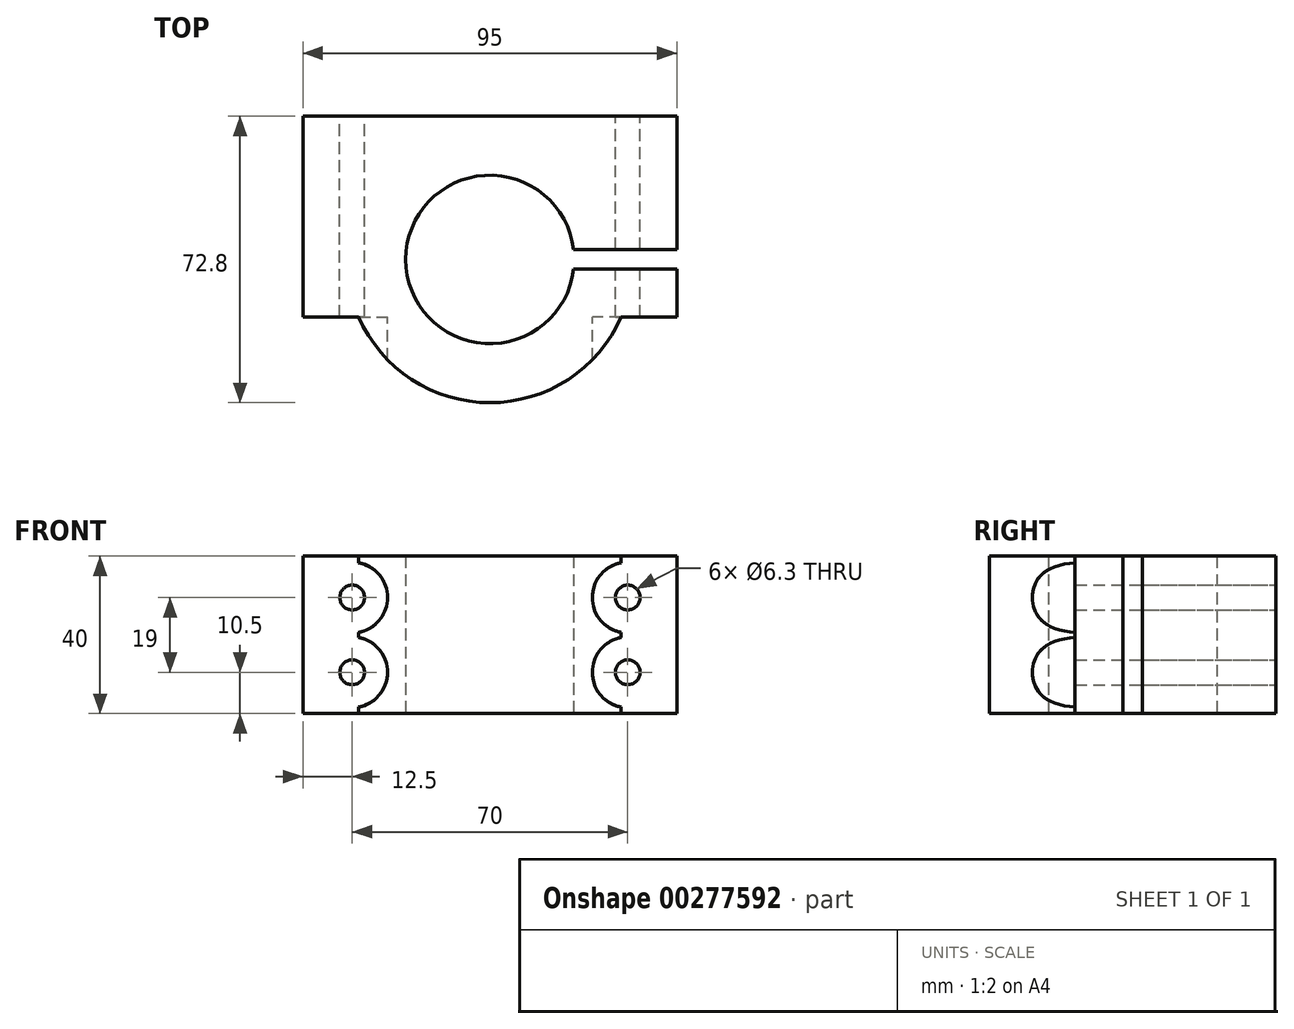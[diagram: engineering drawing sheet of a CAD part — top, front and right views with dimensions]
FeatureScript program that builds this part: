
annotation { "Feature Type Name" : "Feature", "Feature Type Description" : "" }
export const myFeature = defineFeature(function(context is Context, id is Id, definition is map)
    precondition{}
    {
        {
            var Q0;
            Q0=qCreatedBy(makeId("Top.planeOp"),FACE);
            var sketch = newSketch(context, id + "F0", { "sketchPlane" : qUnion([Q0])});
            skLineSegment(sketch, "E0.bottom", {"start": v(47.5, -25.5) * mm, "end": v(-47.5, -25.5) * mm});
            skLineSegment(sketch, "E0.top", {"start": v(47.5, 25.5) * mm, "end": v(-47.5, 25.5) * mm});
            skLineSegment(sketch, "E0.left", {"start": v(47.5, -25.5) * mm, "end": v(47.5, 25.5) * mm});
            skLineSegment(sketch, "E0.right", {"start": v(-47.5, -25.5) * mm, "end": v(-47.5, 25.5) * mm});
            skPoint(sketch, "E0.middle", {"position": v(0, 0) * mm});
            skCircle(sketch, "E1", {"center": v(0, -10.9) * mm, "radius": 21.4 * mm});
            skLineSegment(sketch, "E2.bottom", {"start": v(78.51, -13.4) * mm, "end": v(16, -13.4) * mm});
            skLineSegment(sketch, "E2.top", {"start": v(78.51, -8.4) * mm, "end": v(16, -8.4) * mm});
            skLineSegment(sketch, "E2.left", {"start": v(78.51, -13.4) * mm, "end": v(78.51, -8.4) * mm});
            skLineSegment(sketch, "E2.right", {"start": v(16, -13.4) * mm, "end": v(16, -8.4) * mm});
            skPoint(sketch, "E2.middle", {"position": v(47.25, -10.9) * mm});
            skCircle(sketch, "E3", {"center": v(0, -10.9) * mm, "radius": 36.4 * mm});
            skSolve(sketch);
        }
        {
            var Q0;
            {var subQ0=sQuery(id+"F0.wireOp",EDGE,"E0.right");Q0=makeQuery(id+"F0.imprint","IMPRINT",FACE,{"disambiguationData":[TD([[makeQuery(id+"F0.imprint","IMPRINT",EDGE,{"derivedFrom":subQ0}),-1.0]])]});}
            var Q1;
            {var subQ0=sQuery(id+"F0.wireOp",EDGE,"E0.left");var subQ1=sQuery(id+"F0.wireOp",EDGE,"E0.top");var subQ2=makeQuery(id+"F0.imprint","INTERSECT",VERTEX,{"derivedFrom":[subQ1,subQ0]});Q1=makeQuery(id+"F0.imprint","IMPRINT",FACE,{"disambiguationData":[TD([[makeQuery(id+"F0.imprint","IMPRINT",EDGE,{"disambiguationData":[TD([[subQ2,-1.0]])],"derivedFrom":subQ1}),1.0]])]});}
            var Q2;
            {var subQ0=sQuery(id+"F0.wireOp",EDGE,"E3");var subQ5=sQuery(id+"F0.wireOp",EDGE,"E0.bottom");var subQ8=makeQuery(id+"F0.imprint","INTERSECT",VERTEX,{"disambiguationData":[OD(1.0)],"derivedFrom":[subQ5,subQ0]});Q2=makeQuery(id+"F0.imprint","IMPRINT",FACE,{"disambiguationData":[TD([[makeQuery(id+"F0.imprint","IMPRINT",EDGE,{"disambiguationData":[TD([[subQ8,1.0]])],"derivedFrom":subQ5}),-1.0]])]});}
            var Q3;
            {var subQ0=sQuery(id+"F0.wireOp",EDGE,"E3");var subQ1=sQuery(id+"F0.wireOp",EDGE,"E0.bottom");var subQ2=makeQuery(id+"F0.imprint","INTERSECT",VERTEX,{"disambiguationData":[OD(0.0)],"derivedFrom":[subQ1,subQ0]});Q3=makeQuery(id+"F0.imprint","IMPRINT",FACE,{"disambiguationData":[TD([[makeQuery(id+"F0.imprint","IMPRINT",EDGE,{"disambiguationData":[TD([[subQ2,-1.0]])],"derivedFrom":subQ1}),-1.0]])]});}
            var Q4;
            {var subQ0=sQuery(id+"F0.wireOp",EDGE,"E3");var subQ1=sQuery(id+"F0.wireOp",EDGE,"E0.bottom");var subQ2=makeQuery(id+"F0.imprint","INTERSECT",VERTEX,{"disambiguationData":[OD(0.0)],"derivedFrom":[subQ1,subQ0]});Q4=makeQuery(id+"F0.imprint","IMPRINT",FACE,{"disambiguationData":[TD([[makeQuery(id+"F0.imprint","IMPRINT",EDGE,{"disambiguationData":[TD([[subQ2,-1.0]])],"derivedFrom":subQ1}),1.0]])]});}
            var Q5;
            {var subQ0=sQuery(id+"F0.wireOp",EDGE,"E0.left");var subQ1=sQuery(id+"F0.wireOp",EDGE,"E0.bottom");var subQ2=makeQuery(id+"F0.imprint","INTERSECT",VERTEX,{"derivedFrom":[subQ1,subQ0]});Q5=makeQuery(id+"F0.imprint","IMPRINT",FACE,{"disambiguationData":[TD([[makeQuery(id+"F0.imprint","IMPRINT",EDGE,{"disambiguationData":[TD([[subQ2,-1.0]])],"derivedFrom":subQ1}),-1.0]])]});}
            extrude(context, id + "F1", {"entities" : qUnion([Q0, Q1, Q2, Q3, Q4, Q5]), "depth" : 40 * mm});
        }
        {
            var Q0;
            Q0=makeQuery(id+"F1.opExtrude","SWEPT_FACE",FACE,{"disambiguationData":[OSD([sQuery(id+"F0.wireOp",EDGE,"E0.top")])]});
            var sketch = newSketch(context, id + "F2", { "sketchPlane" : qUnion([Q0])});
            skLineSegment(sketch, "E4.bottom", {"start": v(-35, 29.5) * mm, "end": v(35, 29.5) * mm, "construction": true});
            skLineSegment(sketch, "E4.top", {"start": v(-35, 10.5) * mm, "end": v(35, 10.5) * mm, "construction": true});
            skLineSegment(sketch, "E4.left", {"start": v(-35, 29.5) * mm, "end": v(-35, 10.5) * mm, "construction": true});
            skLineSegment(sketch, "E4.right", {"start": v(35, 29.5) * mm, "end": v(35, 10.5) * mm, "construction": true});
            skCircle(sketch, "E5", {"center": v(-35, 29.5) * mm, "radius": 3.15 * mm});
            skCircle(sketch, "E6", {"center": v(-35, 10.5) * mm, "radius": 3.15 * mm});
            skCircle(sketch, "E7", {"center": v(35, 10.5) * mm, "radius": 3.15 * mm});
            skCircle(sketch, "E8", {"center": v(35, 29.5) * mm, "radius": 3.15 * mm});
            skLineSegment(sketch, "E9", {"start": v(-47.5, 20) * mm, "end": v(-35, 20) * mm, "construction": true});
            skLineSegment(sketch, "E10", {"start": v(47.5, 20) * mm, "end": v(35, 20) * mm, "construction": true});
            skLineSegment(sketch, "E11", {"start": v(0, 10.5) * mm, "end": v(0, 0) * mm, "construction": true});
            skLineSegment(sketch, "E12", {"start": v(0, 29.5) * mm, "end": v(0, 40) * mm, "construction": true});
            skCircle(sketch, "E13", {"center": v(-35, 29.5) * mm, "radius": 9 * mm});
            skCircle(sketch, "E14", {"center": v(-35, 10.5) * mm, "radius": 9 * mm});
            skCircle(sketch, "E15", {"center": v(35, 10.5) * mm, "radius": 9 * mm});
            skCircle(sketch, "E16", {"center": v(35, 29.5) * mm, "radius": 9 * mm});
            skSolve(sketch);
        }
        {
            var Q0;
            Q0=makeQuery(id+"F2.imprint","IMPRINT",FACE,{"disambiguationData":[TD([[makeQuery(id+"F2.imprint","IMPRINT",EDGE,{"derivedFrom":sQuery(id+"F2.wireOp",EDGE,"E5")}),1.0]])]});
            var Q1;
            Q1=makeQuery(id+"F2.imprint","IMPRINT",FACE,{"disambiguationData":[TD([[makeQuery(id+"F2.imprint","IMPRINT",EDGE,{"derivedFrom":sQuery(id+"F2.wireOp",EDGE,"E6")}),1.0]])]});
            var Q2;
            Q2=makeQuery(id+"F2.imprint","IMPRINT",FACE,{"disambiguationData":[TD([[makeQuery(id+"F2.imprint","IMPRINT",EDGE,{"derivedFrom":sQuery(id+"F2.wireOp",EDGE,"E8")}),1.0]])]});
            var Q3;
            Q3=makeQuery(id+"F2.imprint","IMPRINT",FACE,{"disambiguationData":[TD([[makeQuery(id+"F2.imprint","IMPRINT",EDGE,{"derivedFrom":sQuery(id+"F2.wireOp",EDGE,"E7")}),1.0]])]});
            extrude(context, id + "F3", {"entities" : qUnion([Q0, Q1, Q2, Q3]), "operationType" : NewBodyOperationType.REMOVE, "endBound" : BoundingType.THROUGH_ALL, "oppositeDirection" : true, "depth" : 25 * mm});
        }
        {
            var Q0;
            Q0=makeQuery(id+"F2.imprint","IMPRINT",FACE,{"disambiguationData":[TD([[makeQuery(id+"F2.imprint","IMPRINT",EDGE,{"derivedFrom":sQuery(id+"F2.wireOp",EDGE,"E5")}),-1.0]])]});
            var Q1;
            Q1=makeQuery(id+"F2.imprint","IMPRINT",FACE,{"disambiguationData":[TD([[makeQuery(id+"F2.imprint","IMPRINT",EDGE,{"derivedFrom":sQuery(id+"F2.wireOp",EDGE,"E6")}),-1.0]])]});
            var Q2;
            Q2=makeQuery(id+"F2.imprint","IMPRINT",FACE,{"disambiguationData":[TD([[makeQuery(id+"F2.imprint","IMPRINT",EDGE,{"derivedFrom":sQuery(id+"F2.wireOp",EDGE,"E7")}),-1.0]])]});
            var Q3;
            Q3=makeQuery(id+"F2.imprint","IMPRINT",FACE,{"disambiguationData":[TD([[makeQuery(id+"F2.imprint","IMPRINT",EDGE,{"derivedFrom":sQuery(id+"F2.wireOp",EDGE,"E8")}),-1.0]])]});
            var Q4;
            {var subQ0=sQuery(id+"F0.wireOp",EDGE,"E0.bottom");Q4=makeQuery(id+"F1.opExtrude","SWEPT_FACE",FACE,{"disambiguationData":[OSD([subQ0]),TDD([makeQuery(id+"F0.imprint","IMPRINT",EDGE,{"disambiguationData":[TD([[makeQuery(id+"F0.imprint","INTERSECT",VERTEX,{"derivedFrom":[subQ0,sQuery(id+"F0.wireOp",EDGE,"E0.left")]}),-1.0]])],"derivedFrom":subQ0})])]});}
            extrude(context, id + "F4", {"entities" : qUnion([Q0, Q1, Q2, Q3]), "operationType" : NewBodyOperationType.REMOVE, "endBound" : BoundingType.THROUGH_ALL, "oppositeDirection" : true, "depth" : 86.9 * mm, "hasSecondDirection" : true, "secondDirectionBound" : SecondDirectionBoundingType.UP_TO_SURFACE, "secondDirectionOppositeDirection" : true, "secondDirectionBoundEntityFace" : qUnion([Q4]), "secondDirectionDepth" : 53.7 * mm});
        }
    });
